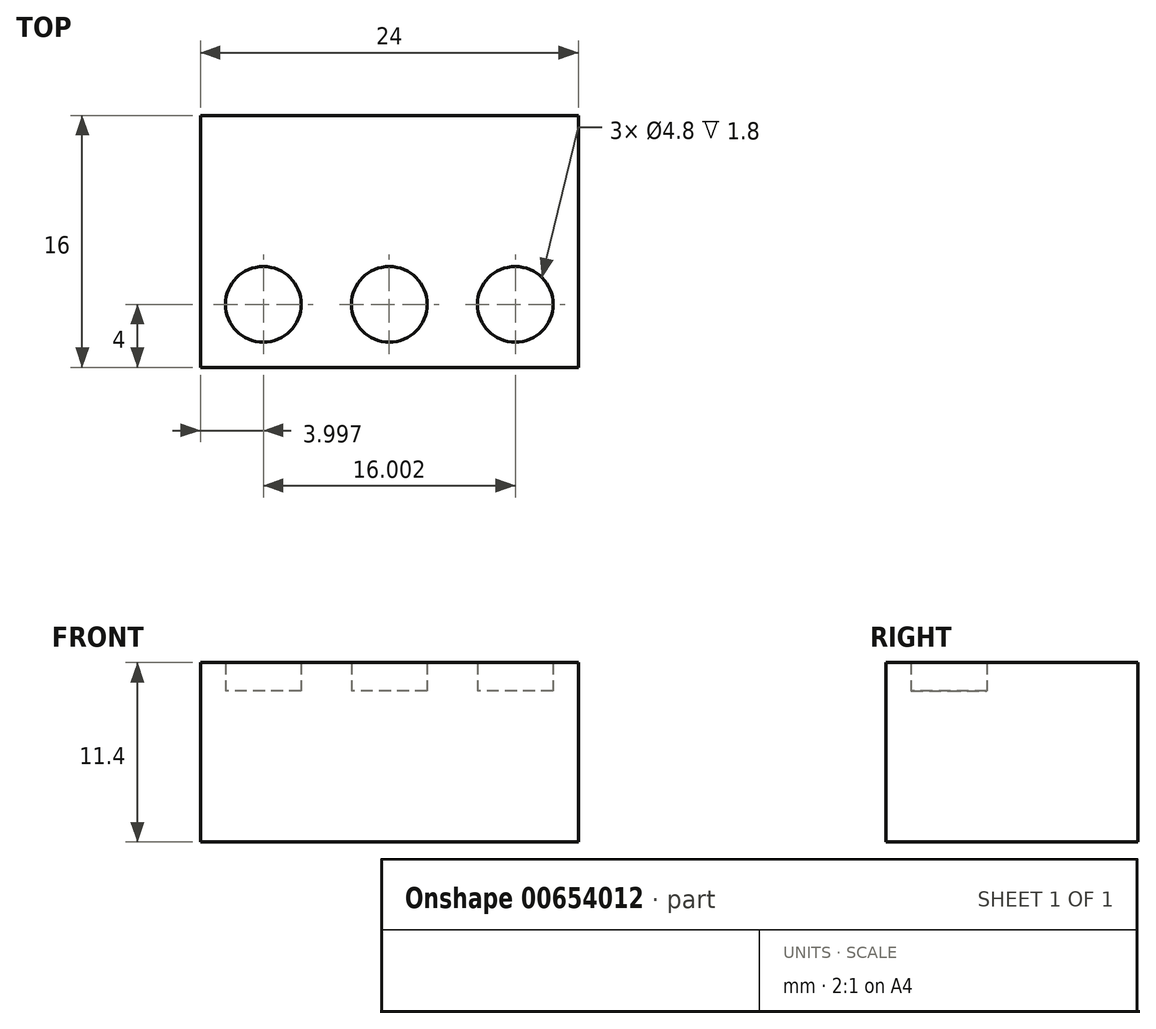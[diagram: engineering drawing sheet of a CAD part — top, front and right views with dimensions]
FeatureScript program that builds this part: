
annotation { "Feature Type Name" : "Feature", "Feature Type Description" : "" }
export const myFeature = defineFeature(function(context is Context, id is Id, definition is map)
    precondition{}
    {
        {
            var Q0;
            Q0=qCreatedBy(makeId("Top.planeOp"),FACE);
            var sketch = newSketch(context, id + "F0", { "sketchPlane" : qUnion([Q0])});
            skLineSegment(sketch, "E0.bottom", {"start": v(0, 0) * mm, "end": v(-24, 0) * mm});
            skLineSegment(sketch, "E0.top", {"start": v(0, 16) * mm, "end": v(-24, 16) * mm});
            skLineSegment(sketch, "E0.left", {"start": v(0, 0) * mm, "end": v(0, 16) * mm});
            skLineSegment(sketch, "E0.right", {"start": v(-24, 0) * mm, "end": v(-24, 16) * mm});
            skSolve(sketch);
        }
        {
            var Q0;
            Q0=makeQuery(id+"F0.imprint","IMPRINT",FACE,{"disambiguationData":[TD([[makeQuery(id+"F0.imprint","IMPRINT",EDGE,{"derivedFrom":sQuery(id+"F0.wireOp",EDGE,"E0.bottom")}),-1.0]])]});
            extrude(context, id + "F1", {"entities" : qUnion([Q0]), "depth" : 9.6 * mm, "offsetDistance" : 25.4 * mm});
        }
        {
            var Q0;
            Q0=makeQuery(id+"F1.opExtrude","CAP_FACE",FACE,{"disambiguationData":[OSD([sQuery(id+"F0.wireOp",EDGE,"E0.bottom"),sQuery(id+"F0.wireOp",EDGE,"E0.top"),sQuery(id+"F0.wireOp",EDGE,"E0.left"),sQuery(id+"F0.wireOp",EDGE,"E0.right")])],"isStart":false});
            var sketch = newSketch(context, id + "F2", { "sketchPlane" : qUnion([Q0])});
            skLineSegment(sketch, "E1", {"start": v(-24, 8) * mm, "end": v(0, 8) * mm, "construction": true});
            skLineSegment(sketch, "E2", {"start": v(-16, 16) * mm, "end": v(-16, 0) * mm, "construction": true});
            skLineSegment(sketch, "E3", {"start": v(-8, 16) * mm, "end": v(-8, 0) * mm, "construction": true});
            skLineSegment(sketch, "E4", {"start": v(-24, 16) * mm, "end": v(-16, 8) * mm, "construction": true});
            skLineSegment(sketch, "E5", {"start": v(-16, 8) * mm, "end": v(-8, 16) * mm, "construction": true});
            skLineSegment(sketch, "E6", {"start": v(-8, 16) * mm, "end": v(0, 8) * mm, "construction": true});
            skCircle(sketch, "E7", {"center": v(-20, 12) * mm, "radius": 2.4 * mm});
            skCircle(sketch, "E8", {"center": v(-12, 12) * mm, "radius": 2.4 * mm});
            skCircle(sketch, "E9", {"center": v(-4, 12) * mm, "radius": 2.4 * mm});
            skCircle(sketch, "E10.MirrorC", {"center": v(-20, 4) * mm, "radius": 2.4 * mm});
            skCircle(sketch, "E11.MirrorC", {"center": v(-12, 4) * mm, "radius": 2.4 * mm});
            skCircle(sketch, "E12.MirrorC", {"center": v(-4, 4) * mm, "radius": 2.4 * mm});
            skSolve(sketch);
        }
        {
            var Q0;
            Q0=makeQuery(id+"F2.imprint","IMPRINT",FACE,{"disambiguationData":[TD([[makeQuery(id+"F2.imprint","IMPRINT",EDGE,{"derivedFrom":sQuery(id+"F2.wireOp",EDGE,"E8")}),1.0]])]});
            var Q1;
            Q1=makeQuery(id+"F2.imprint","IMPRINT",FACE,{"disambiguationData":[TD([[makeQuery(id+"F2.imprint","IMPRINT",EDGE,{"derivedFrom":sQuery(id+"F2.wireOp",EDGE,"E7")}),1.0]])]});
            var Q2;
            Q2=makeQuery(id+"F2.imprint","IMPRINT",FACE,{"disambiguationData":[TD([[makeQuery(id+"F2.imprint","IMPRINT",EDGE,{"derivedFrom":sQuery(id+"F2.wireOp",EDGE,"E9")}),1.0]])]});
            var Q3;
            Q3=makeQuery(id+"F2.imprint","IMPRINT",FACE,{"disambiguationData":[TD([[makeQuery(id+"F2.imprint","IMPRINT",EDGE,{"derivedFrom":sQuery(id+"F2.wireOp",EDGE,"E12.MirrorC")}),-1.0]])]});
            var Q4;
            Q4=makeQuery(id+"F2.imprint","IMPRINT",FACE,{"disambiguationData":[TD([[makeQuery(id+"F2.imprint","IMPRINT",EDGE,{"derivedFrom":sQuery(id+"F2.wireOp",EDGE,"E11.MirrorC")}),-1.0]])]});
            var Q5;
            Q5=makeQuery(id+"F2.imprint","IMPRINT",FACE,{"disambiguationData":[TD([[makeQuery(id+"F2.imprint","IMPRINT",EDGE,{"derivedFrom":sQuery(id+"F2.wireOp",EDGE,"E10.MirrorC")}),-1.0]])]});
            extrude(context, id + "F3", {"entities" : qUnion([Q0, Q1, Q2, Q3, Q4, Q5]), "operationType" : NewBodyOperationType.ADD, "depth" : 1.8 * mm, "offsetDistance" : 25.4 * mm});
        }
    });
